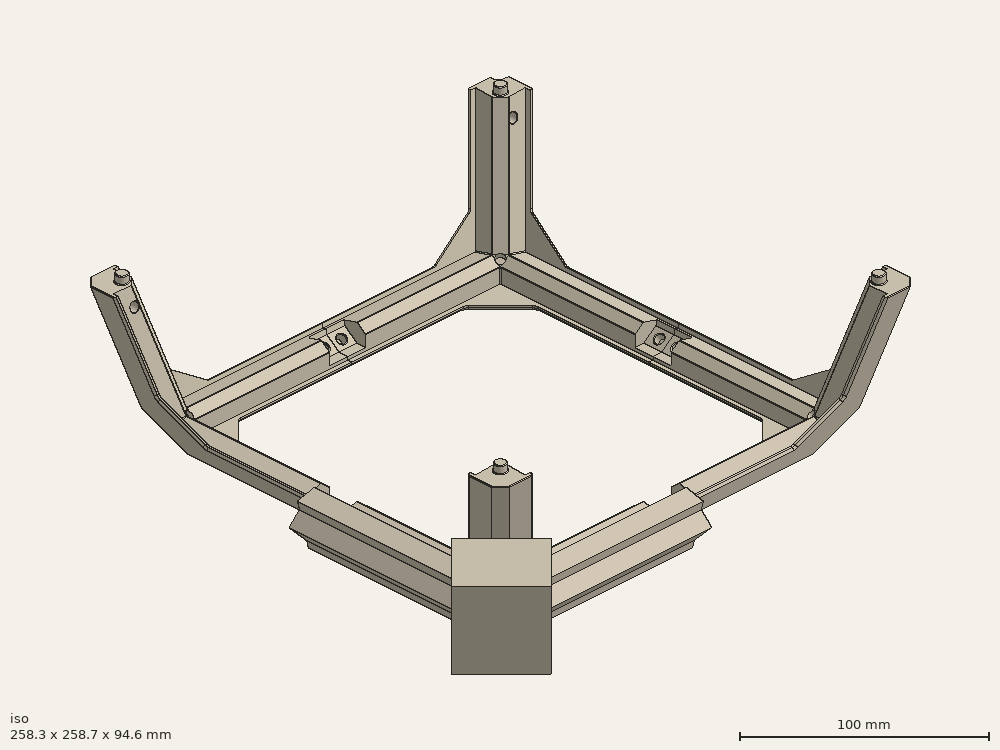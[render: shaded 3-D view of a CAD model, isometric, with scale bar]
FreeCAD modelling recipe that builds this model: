
FCSTD DOCUMENT  (FreeCAD 0.18R16146 (Git))
Label: top-hat-fix
License: All rights reserved
LicenseURL: http://en.wikipedia.org/wiki/All_rights_reserved
objects: Part::Box×11, Part::Feature×9, Part::Chamfer×7, Part::Cut×5, Part::MultiFuse×2
note: 34 computed .brp shape members not serialized (recipe doc carries the construction recipe); baked Part::Feature solids carry a one-line shape summary decoded from their .brp

FEATURE [Part::Feature] Part__Feature998  label="maybe tophat_4_part003"
  Placement = pos=(0,1.7e-14,75) rot=(-1,0,0;1.5708rad)
  shape: bbox 119 x 119 x 79.02 mm, 103 faces (baked)
FEATURE [Part::Feature] Part__Feature995  label="maybe tophat_4_part"
  Placement = pos=(0,1.7e-14,75) rot=(-1,0,0;1.5708rad)
  shape: bbox 119 x 119 x 79.02 mm, 103 faces (baked)
FEATURE [Part::Feature] Part__Feature997  label="maybe tophat_4_part002"
  Placement = pos=(0,1.7e-14,75) rot=(-1,0,0;1.5708rad)
  shape: bbox 119.3 x 119.9 x 79.02 mm, 108 faces (baked)
FEATURE [Part::Box] Box  label="Cube"
  AttacherType = Attacher::AttachEngine3D
  Height = 5
  Length = 103
  Placement = pos=(-103,-103,0) rot=(0,0,1;0rad)
  Width = 7
FEATURE [Part::Box] Box001  label="Cube001"
  AttacherType = Attacher::AttachEngine3D
  Height = 5
  Length = 7
  Placement = pos=(-103,-103,0) rot=(0,0,1;0rad)
  Width = 103
FEATURE [Part::Box] Box002  label="Cube002"
  AttacherType = Attacher::AttachEngine3D
  Height = 10
  Length = 10
  Placement = pos=(-10,-80,0) rot=(0,0,1;0rad)
  Width = 10
FEATURE [Part::Chamfer] Chamfer002
  Base = -> Box002
  Edges = 1 edges r=5: [Edge9]
  Placement = pos=(0,-21,1) rot=(0,0,1;0rad)
FEATURE [Part::Box] Box003  label="Cube003"
  AttacherType = Attacher::AttachEngine3D
  Height = 10
  Length = 10
  Placement = pos=(-82,-10,0) rot=(0,0,1;0rad)
  Width = 10
FEATURE [Part::Chamfer] Chamfer003
  Base = -> Box003
  Edges = 1 edges r=5: [Edge4]
  Placement = pos=(-18,0,1) rot=(0,0,1;0rad)
FEATURE [Part::Box] Box004  label="cut-blk-1"
  AttacherType = Attacher::AttachEngine3D
  Height = 55
  Length = 40
  Placement = pos=(-125.988,-98.1175,-15.5935) rot=(0.386624,-0.160145,-0.908227;0.855778rad)
  Width = 25
FEATURE [Part::Box] Box005  label="cut-blk-002"
  AttacherType = Attacher::AttachEngine3D
  Height = 55
  Length = 40
  Placement = pos=(-125.988,-98.1175,-15.5935) rot=(0.386624,-0.160145,-0.908227;0.855778rad)
  Width = 25
FEATURE [Part::Box] Box006  label="cut-blk-003"
  AttacherType = Attacher::AttachEngine3D
  Height = 55
  Length = 40
  Placement = pos=(-125.988,-98.1175,-15.5935) rot=(0.386624,-0.160145,-0.908227;0.855778rad)
  Width = 25
FEATURE [Part::Box] Box008  label="Cube005"
  AttacherType = Attacher::AttachEngine3D
  Height = 25
  Length = 105
  Placement = pos=(-105,-109.104,-4.15384) rot=(1,0,0;0.251851rad)
  Width = 10
FEATURE [Part::Feature] Box008001  label="Cube006"
  Placement = pos=(0.01,-105,0) rot=(0,0,-1;1.5708rad)
  shape: bbox 15.91 x 105 x 26.7 mm, 6 faces (baked)
FEATURE [Part::Box] Box008002  label="Cube007"
  AttacherType = Attacher::AttachEngine3D
  Height = 27
  Length = 103
  Placement = pos=(-103,-101.027,-9.34088) rot=(1,0,0;0.785398rad)
  Width = 10
FEATURE [Part::Feature] Box008002001  label="Cube008"
  Placement = pos=(0.01,-103,0) rot=(0,0,-1;1.5708rad)
  shape: bbox 26.16 x 103 x 26.16 mm, 6 faces (baked)
FEATURE [Part::Feature] Part__Feature996  label="maybe tophat_4_part001"
  Placement = pos=(0,1.7e-14,75) rot=(-1,0,0;1.5708rad)
  shape: bbox 119 x 119 x 79.02 mm, 103 faces (baked)
FEATURE [Part::Box] Box007  label="Cube004"
  AttacherType = Attacher::AttachEngine3D
  Height = 19
  Length = 36
  Placement = pos=(-114.815,-89.3588,0) rot=(0,0,1;5.49779rad)
  Width = 26
FEATURE [Part::Chamfer] Chamfer001
  Base = -> Box001
  Edges = 1 edges r=4.84: [Edge4]
  Placement = pos=(1.93,0,0) rot=(0,0,1;0rad)
FEATURE [Part::Cut] Cut001
  Base = -> Chamfer001
  Tool = -> Chamfer003
FEATURE [Part::Cut] Cut003
  Base = -> Cut001
  Tool = -> Box004
FEATURE [Part::Chamfer] Chamfer
  Base = -> Box
  Edges = 1 edges r=4.84: [Edge9]
  Placement = pos=(0,1.93,0) rot=(0,0,1;0rad)
FEATURE [Part::Cut] Cut
  Base = -> Chamfer
  Tool = -> Chamfer002
FEATURE [Part::MultiFuse] Fusion
  Shapes = -> [Cut003,Cut]
FEATURE [Part::Box] Box008002003  label="Cube010"
  AttacherType = Attacher::AttachEngine3D
  Height = 19
  Length = 32
  Placement = pos=(-93.5095,-135.936,0) rot=(0,0,1;0.785398rad)
  Width = 60
FEATURE [Part::Cut] Cut004
  Base = -> Fusion
  Tool = -> Box008002003
FEATURE [Part::Chamfer] Chamfer004
  Base = -> Box007
  Edges = 2 edges r=14.3: [Edge1,Edge5]
FEATURE [Part::Feature] Chamfer004001  label="Chamfer005"
  shape: bbox 33.73 x 33.73 x 19 mm, 8 faces (baked)
FEATURE [Part::Chamfer] Chamfer004002
  Base = -> Chamfer004
  Edges = 3 edges r=8.45: [Edge10,Edge14,Edge16]
FEATURE [Part::Chamfer] Chamfer004003
  Base = -> Chamfer004002
  Edges = 2 edges: [Edge1 r1=5.2 r2=20.2,Edge23 r1=5.2 r2=20.2]
FEATURE [Part::MultiFuse] Fusion001
  Shapes = -> [Chamfer004003,Cut004]
FEATURE [Part::Feature] Fusion001001  label="Fusion002"
  shape: bbox 104.7 x 104.7 x 19 mm, 33 faces (baked)
FEATURE [Part::Feature] Chamfer004004001  label="Chamfer004005"
  shape: bbox 41.01 x 41.01 x 32 mm, 8 faces (baked)
FEATURE [Part::Cut] Cut005
  Base = -> Fusion001001
  Tool = -> Chamfer004004001
